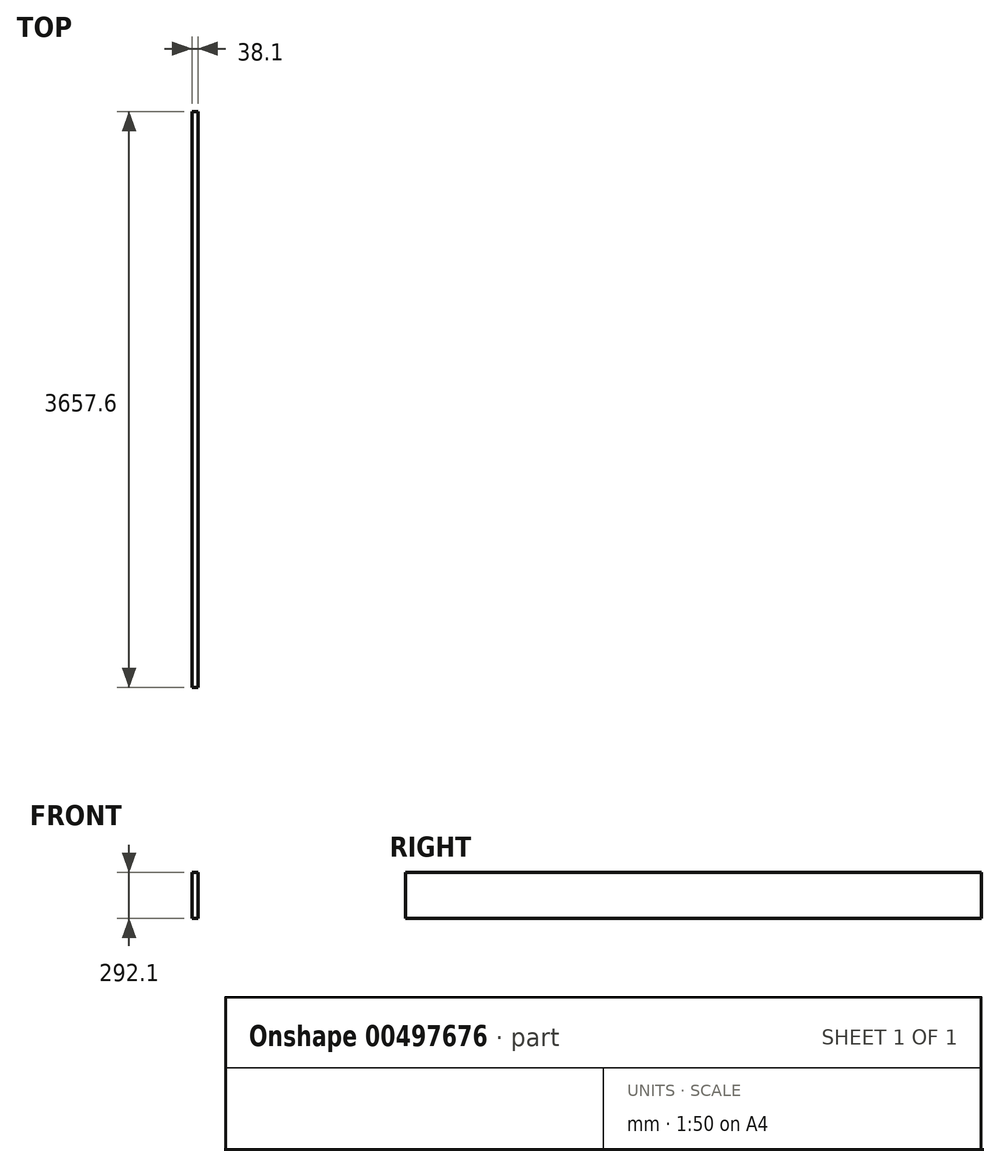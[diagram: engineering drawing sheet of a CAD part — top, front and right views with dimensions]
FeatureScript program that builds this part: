
annotation { "Feature Type Name" : "Feature", "Feature Type Description" : "" }
export const myFeature = defineFeature(function(context is Context, id is Id, definition is map)
    precondition{}
    {
        {
            var Q0;
            Q0=qCreatedBy(makeId("Front.planeOp"),FACE);
            var sketch = newSketch(context, id + "F0", { "sketchPlane" : qUnion([Q0])});
            skLineSegment(sketch, "E0.bottom", {"start": v(0, 0) * mm, "end": v(38.1, 0) * mm});
            skLineSegment(sketch, "E0.top", {"start": v(0, 292.1) * mm, "end": v(38.1, 292.1) * mm});
            skLineSegment(sketch, "E0.left", {"start": v(0, 0) * mm, "end": v(0, 292.1) * mm});
            skLineSegment(sketch, "E0.right", {"start": v(38.1, 0) * mm, "end": v(38.1, 292.1) * mm});
            skSolve(sketch);
        }
        {
            var Q0;
            Q0 = qSketchRegion(id + "F0", true);
            extrude(context, id + "F1", {"entities" : qUnion([Q0]), "depth" : 3657.6 * mm});
        }
    });
